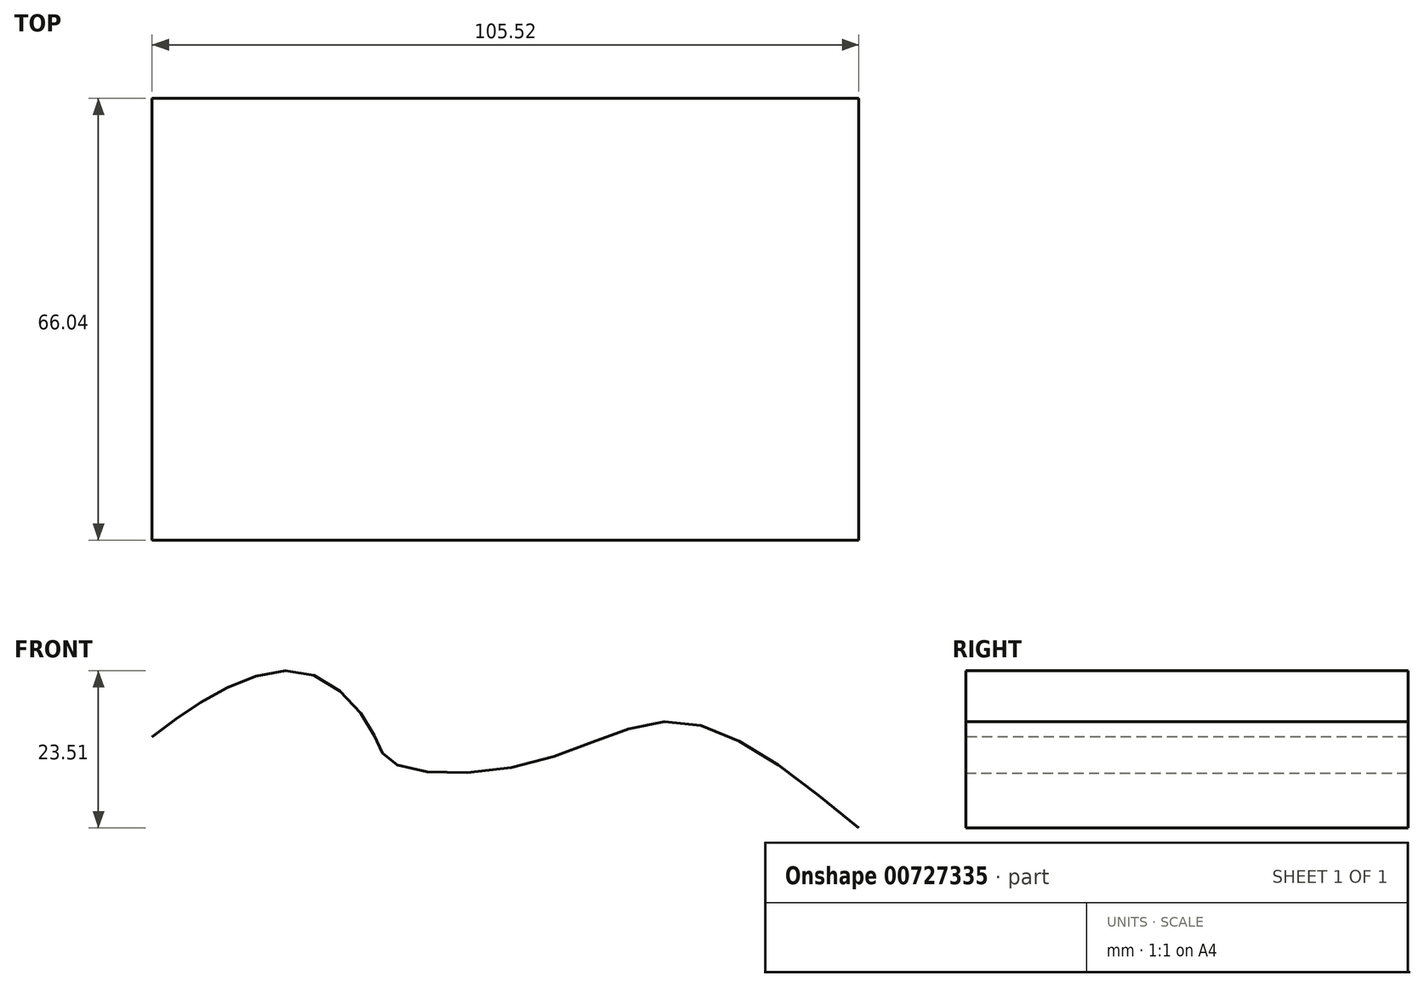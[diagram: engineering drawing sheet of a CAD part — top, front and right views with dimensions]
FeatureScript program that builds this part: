
annotation { "Feature Type Name" : "Feature", "Feature Type Description" : "" }
export const myFeature = defineFeature(function(context is Context, id is Id, definition is map)
    precondition{}
    {
        {
            var Q0;
            Q0=qCreatedBy(makeId("Front.planeOp"),FACE);
            var sketch = newSketch(context, id + "F0", { "sketchPlane" : qUnion([Q0])});
            skFitSpline(sketch, "E0", {"points": [v(0, 0) * mm, v(-26.74, 15.85) * mm, v(-48.52, 9.77) * mm, v(-69.66, 9.77) * mm, v(-72.54, 14.25) * mm, v(-81.5, 22.9) * mm, v(-94.31, 20.98) * mm, v(-105.52, 13.61) * mm], "startDerivative": vector(-138.97, 114.57) * mm, "endDerivative": vector(-81.13, -61.21) * mm});
            skSolve(sketch);
        }
        {
            var Q0;
            Q0=sQuery(id+"F0.wireOp",EDGE,"E0");
            extrude(context, id + "F1", {"bodyType" : ToolBodyType.SURFACE, "surfaceEntities" : qUnion([Q0]), "depth" : 66.04 * mm, "offsetDistance" : 25.4 * mm});
        }
    });
